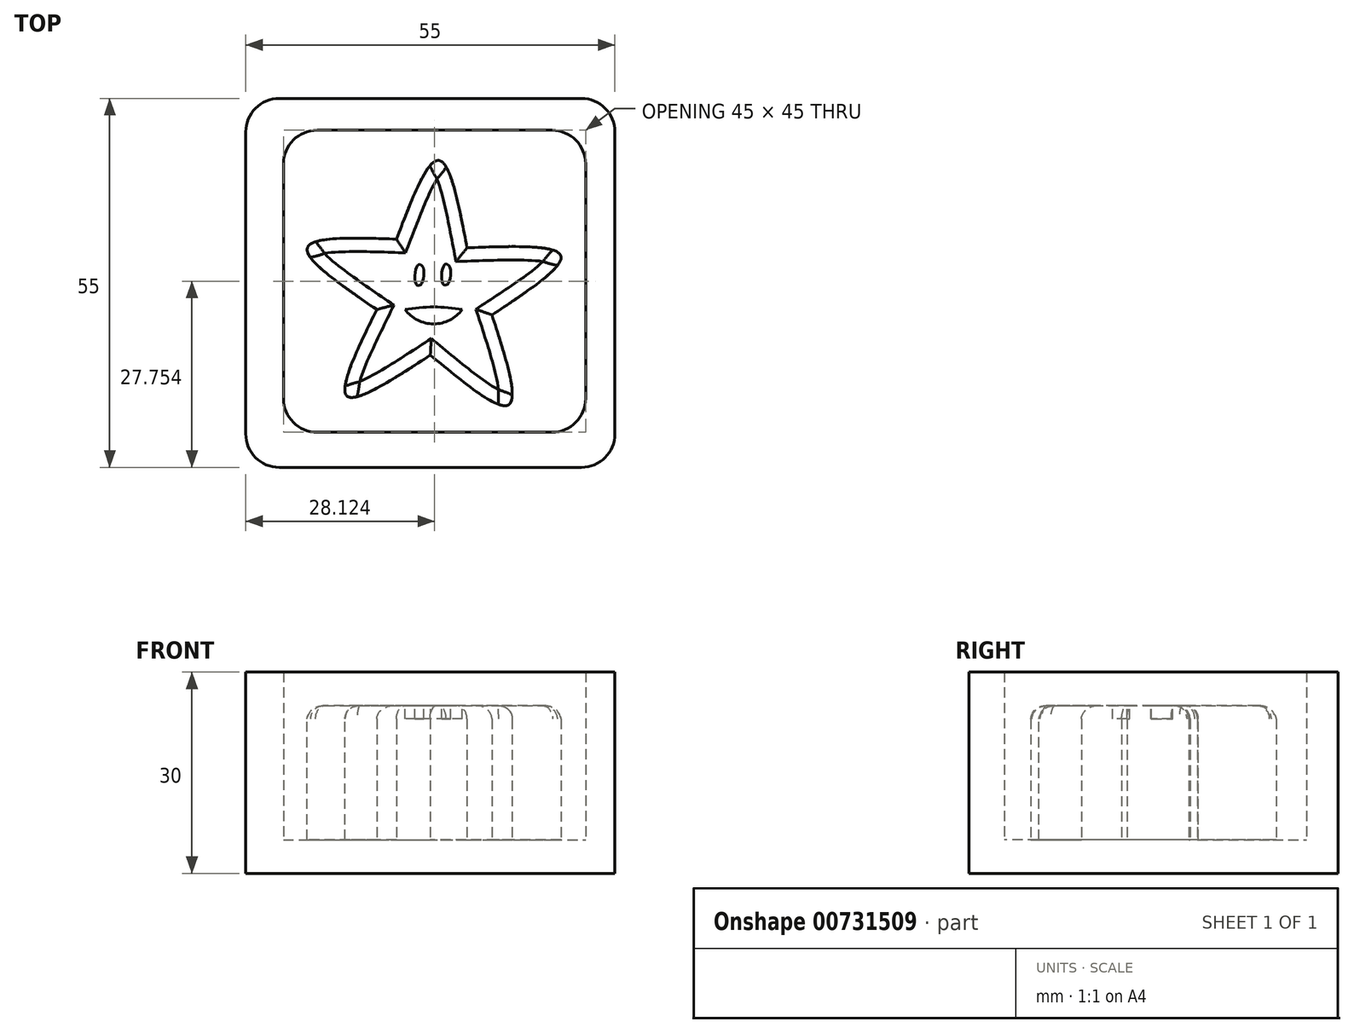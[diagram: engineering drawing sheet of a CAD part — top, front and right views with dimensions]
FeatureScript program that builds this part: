
annotation { "Feature Type Name" : "Feature", "Feature Type Description" : "" }
export const myFeature = defineFeature(function(context is Context, id is Id, definition is map)
    precondition{}
    {
        {
            var Q0;
            Q0=qCreatedBy(makeId("Top.planeOp"),FACE);
            var sketch = newSketch(context, id + "F0", { "sketchPlane" : qUnion([Q0])});
            skLineSegment(sketch, "E0.bottom", {"start": v(25, -20.84) * mm, "end": v(-25, -20.84) * mm});
            skLineSegment(sketch, "E0.top", {"start": v(25, 29.16) * mm, "end": v(-25, 29.16) * mm});
            skLineSegment(sketch, "E0.left", {"start": v(25, -20.84) * mm, "end": v(25, 29.16) * mm});
            skLineSegment(sketch, "E0.right", {"start": v(-25, -20.84) * mm, "end": v(-25, 29.16) * mm});
            skPoint(sketch, "E0.middle", {"position": v(0, 4.16) * mm});
            skSolve(sketch);
        }
        {
            var Q0;
            Q0 = qSketchRegion(id + "F0", true);
            extrude(context, id + "F1", {"entities" : qUnion([Q0]), "depth" : 5 * mm, "offsetDistance" : 25 * mm});
        }
        {
            var Q0;
            Q0=makeQuery(id+"F1.opExtrude","CAP_FACE",FACE,{"disambiguationData":[OSD([sQuery(id+"F0.wireOp",EDGE,"E0.bottom"),sQuery(id+"F0.wireOp",EDGE,"E0.top"),sQuery(id+"F0.wireOp",EDGE,"E0.left"),sQuery(id+"F0.wireOp",EDGE,"E0.right")])],"isStart":false});
            var sketch = newSketch(context, id + "F2", { "sketchPlane" : qUnion([Q0])});
            skFitSpline(sketch, "E1", {"points": [v(-5.06, 10.5) * mm, v(1.24, 22.23) * mm, v(5.46, 9.21) * mm], "startDerivative": vector(13.75, 35.91) * mm, "endDerivative": vector(7.31, -38.33) * mm});
            skFitSpline(sketch, "E2", {"points": [v(5.46, 9.21) * mm, v(19.44, 8) * mm, v(9.17, -0.8) * mm], "startDerivative": vector(39.9, 1.48) * mm, "endDerivative": vector(-32.7, -21.56) * mm});
            skFitSpline(sketch, "E3", {"points": [v(9.17, -0.8) * mm, v(11.68, -14.18) * mm, v(0, -6.8) * mm], "startDerivative": vector(12.08, -37.22) * mm, "endDerivative": vector(-30.37, 25.15) * mm});
            skFitSpline(sketch, "E4", {"points": [v(-5.06, 10.5) * mm, v(-18.32, 9.21) * mm, v(-7.98, 0) * mm], "startDerivative": vector(-38.48, 1.26) * mm, "endDerivative": vector(32.4, -22.2) * mm});
            skFitSpline(sketch, "E5", {"points": [v(-7.98, 0) * mm, v(-12.41, -12.88) * mm, v(0, -6.8) * mm], "startDerivative": vector(-17.27, -35.33) * mm, "endDerivative": vector(33.18, 21.68) * mm});
            skSolve(sketch);
        }
        {
            var Q0;
            Q0 = qSketchRegion(id + "F2", true);
            extrude(context, id + "F3", {"entities" : qUnion([Q0]), "operationType" : NewBodyOperationType.ADD, "depth" : 20 * mm, "offsetDistance" : 25 * mm});
        }
        {
            var Q0;
            Q0=makeQuery(id+"F3.opExtrude","CAP_EDGE",EDGE,{"disambiguationData":[OSD([sQuery(id+"F2.wireOp",EDGE,"E4")])],"isStart":false});
            var Q1;
            Q1=makeQuery(id+"F3.opExtrude","CAP_EDGE",EDGE,{"disambiguationData":[OSD([sQuery(id+"F2.wireOp",EDGE,"E5")])],"isStart":false});
            var Q2;
            Q2=makeQuery(id+"F3.opExtrude","CAP_EDGE",EDGE,{"disambiguationData":[OSD([sQuery(id+"F2.wireOp",EDGE,"E3")])],"isStart":false});
            var Q3;
            Q3=makeQuery(id+"F3.opExtrude","CAP_EDGE",EDGE,{"disambiguationData":[OSD([sQuery(id+"F2.wireOp",EDGE,"E2")])],"isStart":false});
            var Q4;
            Q4=makeQuery(id+"F3.opExtrude","CAP_EDGE",EDGE,{"disambiguationData":[OSD([sQuery(id+"F2.wireOp",EDGE,"E1")])],"isStart":false});
            fillet(context, id + "F4", {"entities" : qUnion([Q0, Q1, Q2, Q3, Q4]), "radius" : 2 * mm, "tangentPropagation" : true, "allowEdgeOverflow" : false});
        }
        {
            var Q0;
            Q0=qCreatedBy(makeId("Top.planeOp"),FACE);
            var sketch = newSketch(context, id + "F5", { "sketchPlane" : qUnion([Q0])});
            skLineSegment(sketch, "E6.bottom", {"start": v(27.5, -23.53) * mm, "end": v(-27.5, -23.53) * mm});
            skLineSegment(sketch, "E6.top", {"start": v(27.5, 31.47) * mm, "end": v(-27.5, 31.47) * mm});
            skLineSegment(sketch, "E6.left", {"start": v(27.5, -23.53) * mm, "end": v(27.5, 31.47) * mm});
            skLineSegment(sketch, "E6.right", {"start": v(-27.5, -23.53) * mm, "end": v(-27.5, 31.47) * mm});
            skPoint(sketch, "E6.middle", {"position": v(0, 3.97) * mm});
            skLineSegment(sketch, "E7.bottom", {"start": v(23.12, -18.28) * mm, "end": v(-21.88, -18.28) * mm});
            skLineSegment(sketch, "E7.top", {"start": v(23.12, 26.72) * mm, "end": v(-21.88, 26.72) * mm});
            skLineSegment(sketch, "E7.left", {"start": v(23.12, -18.28) * mm, "end": v(23.12, 26.72) * mm});
            skLineSegment(sketch, "E7.right", {"start": v(-21.88, -18.28) * mm, "end": v(-21.88, 26.72) * mm});
            skPoint(sketch, "E7.middle", {"position": v(0, 3.98) * mm});
            skSolve(sketch);
        }
        {
            var Q0;
            Q0 = qSketchRegion(id + "F5", true);
            extrude(context, id + "F6", {"entities" : qUnion([Q0]), "operationType" : NewBodyOperationType.ADD, "depth" : 30 * mm, "offsetDistance" : 25 * mm});
        }
        {
            var Q0;
            Q0=makeQuery(id+"F6.opExtrude","SWEPT_EDGE",EDGE,{"disambiguationData":[OSD([sQuery(id+"F5.wireOp",EDGE,"E7.top"),sQuery(id+"F5.wireOp",EDGE,"E7.left")])]});
            var Q1;
            Q1=makeQuery(id+"F6.opExtrude","SWEPT_EDGE",EDGE,{"disambiguationData":[OSD([sQuery(id+"F5.wireOp",EDGE,"E7.bottom"),sQuery(id+"F5.wireOp",EDGE,"E7.left")])]});
            var Q2;
            Q2=makeQuery(id+"F6.opExtrude","SWEPT_EDGE",EDGE,{"disambiguationData":[OSD([sQuery(id+"F5.wireOp",EDGE,"E7.top"),sQuery(id+"F5.wireOp",EDGE,"E7.right")])]});
            var Q3;
            Q3=makeQuery(id+"F6.opExtrude","SWEPT_EDGE",EDGE,{"disambiguationData":[OSD([sQuery(id+"F5.wireOp",EDGE,"E7.bottom"),sQuery(id+"F5.wireOp",EDGE,"E7.right")])]});
            fillet(context, id + "F7", {"entities" : qUnion([Q0, Q1, Q2, Q3]), "radius" : 5 * mm, "tangentPropagation" : true, "allowEdgeOverflow" : false});
        }
        {
            var Q0;
            Q0=makeQuery(id+"F6.opExtrude","SWEPT_EDGE",EDGE,{"disambiguationData":[OSD([sQuery(id+"F5.wireOp",EDGE,"E6.top"),sQuery(id+"F5.wireOp",EDGE,"E6.right")])]});
            var Q1;
            Q1=makeQuery(id+"F6.opExtrude","SWEPT_EDGE",EDGE,{"disambiguationData":[OSD([sQuery(id+"F5.wireOp",EDGE,"E6.top"),sQuery(id+"F5.wireOp",EDGE,"E6.left")])]});
            var Q2;
            Q2=makeQuery(id+"F6.opExtrude","SWEPT_EDGE",EDGE,{"disambiguationData":[OSD([sQuery(id+"F5.wireOp",EDGE,"E6.bottom"),sQuery(id+"F5.wireOp",EDGE,"E6.right")])]});
            var Q3;
            Q3=makeQuery(id+"F6.opExtrude","SWEPT_EDGE",EDGE,{"disambiguationData":[OSD([sQuery(id+"F5.wireOp",EDGE,"E6.bottom"),sQuery(id+"F5.wireOp",EDGE,"E6.left")])]});
            fillet(context, id + "F8", {"entities" : qUnion([Q0, Q1, Q2, Q3]), "radius" : 5 * mm, "tangentPropagation" : true, "allowEdgeOverflow" : false});
        }
        {
            var Q0;
            Q0=makeQuery(id+"F3.opExtrude","CAP_FACE",FACE,{"disambiguationData":[OSD([sQuery(id+"F2.wireOp",EDGE,"ea22f027-b894-4d35-ad94-6574a105fb3a"),sQuery(id+"F2.wireOp",EDGE,"02972ecb-89ef-400d-9b9c-b38da18b9f26"),sQuery(id+"F2.wireOp",EDGE,"d4665c4b-3644-410e-b7a9-793b46f9e3d8"),sQuery(id+"F2.wireOp",EDGE,"4904a858-6bfa-4176-8c43-c28e2eb22261"),sQuery(id+"F2.wireOp",EDGE,"281288f6-0dfc-4ab6-aa52-0887e6a29920"),sQuery(id+"F2.wireOp",EDGE,"e6a59349-29be-4dfa-85ae-5f5bb5e19001"),sQuery(id+"F2.wireOp",EDGE,"33865bf9-fee0-4887-a290-a33334908563"),sQuery(id+"F2.wireOp",EDGE,"b5a1ea3e-0a3a-46d1-a9d2-b11f3d4d393f"),sQuery(id+"F2.wireOp",EDGE,"9160b71b-1dbf-454e-b8aa-38d11ad0787a"),sQuery(id+"F2.wireOp",EDGE,"508b1097-dadd-43a8-a367-845bdcffccfe"),sQuery(id+"F2.wireOp",EDGE,"49bc861f-a654-40ca-8a3d-e641ddbf638b"),sQuery(id+"F2.wireOp",EDGE,"b91fa5d4-4bf4-43ae-99f3-f47139d4a982"),sQuery(id+"F2.wireOp",EDGE,"91c30a01-8c2e-4a9e-bc94-6af126d221bb"),sQuery(id+"F2.wireOp",EDGE,"46226220-93ab-4b08-822d-1d4fcd13f7f0"),sQuery(id+"F2.wireOp",EDGE,"3cccdf76-d96c-4aba-a423-c60eeaef6f2e"),sQuery(id+"F2.wireOp",EDGE,"a7a83c28-3530-49f8-9c53-c2483f9e7872"),sQuery(id+"F2.wireOp",EDGE,"bd418752-b331-4a27-85c2-437b8f3f9da8"),sQuery(id+"F2.wireOp",EDGE,"d86c6e9c-a8e8-46bc-9cbd-8a8ccbf43cd8"),sQuery(id+"F2.wireOp",EDGE,"18ce2d2a-cbe7-4d55-9af2-434ca90d4d8a"),sQuery(id+"F2.wireOp",EDGE,"3e9cf44d-97a5-4047-a5a6-f93e2a769566"),sQuery(id+"F2.wireOp",EDGE,"72104b77-425f-43ce-bfee-662c898d3039"),sQuery(id+"F2.wireOp",EDGE,"b0c94266-c951-4a47-ba1d-05842cc99b57"),sQuery(id+"F2.wireOp",EDGE,"a3bab185-7591-47d8-8c31-848ac42d466f"),sQuery(id+"F2.wireOp",EDGE,"95482d24-3030-4f51-9019-3cd7c5544abc"),sQuery(id+"F2.wireOp",EDGE,"ecb43bb9-7518-4037-82ed-3b3d48b88220"),sQuery(id+"F2.wireOp",EDGE,"6709acc4-015e-4cee-b4b1-e8162d60af49"),sQuery(id+"F2.wireOp",EDGE,"9c087dd5-8d5f-4c13-9bc7-0dec2b4ae27f"),sQuery(id+"F2.wireOp",EDGE,"1f7cd400-eb1a-477a-a8e0-1a1905c8875b"),sQuery(id+"F2.wireOp",EDGE,"2f4714a1-4b7a-4e27-a0f3-d2b64ee53851"),sQuery(id+"F2.wireOp",EDGE,"cf6d8417-590a-48c5-99af-b32b253a895c"),sQuery(id+"F2.wireOp",EDGE,"93dc3e3c-f9e4-4bb0-b6ea-1e3b1bb8eda1"),sQuery(id+"F2.wireOp",EDGE,"f410118d-9d75-4c7b-a8da-20c13fada343"),sQuery(id+"F2.wireOp",EDGE,"eae4d265-d466-4ba0-ad54-7133bb8090aa"),sQuery(id+"F2.wireOp",EDGE,"29f3a1ae-a44a-4252-90b8-49e4f717a763"),sQuery(id+"F2.wireOp",EDGE,"d95e87fc-c752-4cd3-ba2f-4e1b622d11e6"),sQuery(id+"F2.wireOp",EDGE,"42a256c7-bd9f-4b82-a40e-3aa7b43a7311"),sQuery(id+"F2.wireOp",EDGE,"5cccd7cb-d227-495f-bd2e-dd321fa3711f"),sQuery(id+"F2.wireOp",EDGE,"4779d78b-67a4-4074-8e1d-094c3c882748"),sQuery(id+"F2.wireOp",EDGE,"d78c889f-446d-499c-940c-2d769212d2d6"),sQuery(id+"F2.wireOp",EDGE,"5978d452-f883-4c3a-89cf-e77a3d4812d3"),sQuery(id+"F2.wireOp",EDGE,"d596c75f-4af1-4a7b-b4a9-307fc33695f2"),sQuery(id+"F2.wireOp",EDGE,"ac6da6d2-c422-4b3f-ab3b-024f16e2174f"),sQuery(id+"F2.wireOp",EDGE,"f701fbac-f9f2-41ce-b398-1cdb972a07c6"),sQuery(id+"F2.wireOp",EDGE,"6ea0370e-b9df-47c8-82b6-4bf531107383"),sQuery(id+"F2.wireOp",EDGE,"93d4d691-acf9-4093-813e-c243a6abfd77"),sQuery(id+"F2.wireOp",EDGE,"564c231c-7281-4956-8916-2b9847646294"),sQuery(id+"F2.wireOp",EDGE,"447afba2-fe07-4bf1-a098-a2fa503544db"),sQuery(id+"F2.wireOp",EDGE,"783018d8-4da7-439e-baff-4ea1af6aeaae"),sQuery(id+"F2.wireOp",EDGE,"23360fc8-9112-4eab-be8c-d36215a4c504"),sQuery(id+"F2.wireOp",EDGE,"f39823fe-76bf-4b28-8de3-5866c156ca6e"),sQuery(id+"F2.wireOp",EDGE,"94261188-8fe8-4fe3-9cfb-41c0c768c078"),sQuery(id+"F2.wireOp",EDGE,"639eefb3-3c81-4241-8da9-6294a00eecad"),sQuery(id+"F2.wireOp",EDGE,"63a26b51-3e8c-4d7f-a8c5-c852ed6635fd"),sQuery(id+"F2.wireOp",EDGE,"0cbcce5a-d863-44dc-85fc-889f0cb27286"),sQuery(id+"F2.wireOp",EDGE,"41481716-7baf-47e6-bab9-346e36ad7ed7"),sQuery(id+"F2.wireOp",EDGE,"a0ece215-4608-46fb-b9de-0966884f3722"),sQuery(id+"F2.wireOp",EDGE,"cea85d6a-f16e-43e1-82ab-1eb20eedc667"),sQuery(id+"F2.wireOp",EDGE,"90b3652e-c92f-4129-b232-5fc3862136ad"),sQuery(id+"F2.wireOp",EDGE,"d85ff010-6106-4afe-aa78-55669356d399"),sQuery(id+"F2.wireOp",EDGE,"7b3810e8-a3aa-46c5-9845-10c95717e511"),sQuery(id+"F2.wireOp",EDGE,"32d08b1a-e728-49a8-914d-c4ecc0554df0"),sQuery(id+"F2.wireOp",EDGE,"a932f2cb-edb6-4d43-8a31-36080f450e31"),sQuery(id+"F2.wireOp",EDGE,"6d77b220-5459-4ded-ba71-0805bf8e97fe"),sQuery(id+"F2.wireOp",EDGE,"d4a3d79f-eb9b-45d3-af4d-7f6e0c1d0b6a"),sQuery(id+"F2.wireOp",EDGE,"3a8167d0-93d4-4fee-93fc-e765f78cc71a"),sQuery(id+"F2.wireOp",EDGE,"275b4ef8-3749-467f-b8de-4c5ca6efd012"),sQuery(id+"F2.wireOp",EDGE,"250f3aee-73fb-4a09-89d3-a25958f34bab"),sQuery(id+"F2.wireOp",EDGE,"6f7494f2-175a-490b-9ca9-9ab7524c1492"),sQuery(id+"F2.wireOp",EDGE,"d4bde236-d2fc-4dbc-ba9a-6cd55d3f6a15"),sQuery(id+"F2.wireOp",EDGE,"989c9d0c-4ceb-449c-bc73-c96cc92b2f1a"),sQuery(id+"F2.wireOp",EDGE,"78fda69b-8c10-4e3c-872b-102a69ddef83"),sQuery(id+"F2.wireOp",EDGE,"a15857fb-2d82-4afa-8e36-ecf18161f336"),sQuery(id+"F2.wireOp",EDGE,"b5dc66a1-7abf-40bc-8f4a-394b90f8d275"),sQuery(id+"F2.wireOp",EDGE,"03030db5-3b63-482b-9307-c4991d58ca64"),sQuery(id+"F2.wireOp",EDGE,"17e9b168-3d8f-465c-93a2-82195902c407"),sQuery(id+"F2.wireOp",EDGE,"7465df75-a5ab-45e8-a90a-397120fadcc2"),sQuery(id+"F2.wireOp",EDGE,"16613f2c-828e-433e-977f-464dc0bab4c5"),sQuery(id+"F2.wireOp",EDGE,"47fe3ba8-9260-47cb-bf79-68fdcf4e78a0"),sQuery(id+"F2.wireOp",EDGE,"43b05b75-3a74-4bef-b5f9-64ce1e4d3f92"),sQuery(id+"F2.wireOp",EDGE,"991257b0-d842-40bd-a016-b0dcd5567a51"),sQuery(id+"F2.wireOp",EDGE,"bb4ff494-dc7b-4f0b-a60d-949d5af28021"),sQuery(id+"F2.wireOp",EDGE,"be03492f-4681-4838-bb13-d5d06ba2e1d7"),sQuery(id+"F2.wireOp",EDGE,"97411946-2583-4f17-b8cd-8f9e6a677e8b"),sQuery(id+"F2.wireOp",EDGE,"e440f547-cbda-46c2-b9d7-514191ae65e8"),sQuery(id+"F2.wireOp",EDGE,"60f7c09c-a596-4b98-aa55-1e6369aacef9"),sQuery(id+"F2.wireOp",EDGE,"234aff2d-32ac-438c-92f5-d0bf77c84f1a"),sQuery(id+"F2.wireOp",EDGE,"b87faba7-c0e6-491b-a4a2-d00cc7015cd8"),sQuery(id+"F2.wireOp",EDGE,"90d1a113-3cec-4f00-adab-2e55525ea2b2"),sQuery(id+"F2.wireOp",EDGE,"979cd316-eb47-42a9-a592-d31acdb67cec"),sQuery(id+"F2.wireOp",EDGE,"7428ea2a-103f-4ebb-b4b8-c831fed82aef"),sQuery(id+"F2.wireOp",EDGE,"52370307-3d29-4edd-afa2-faff63602114"),sQuery(id+"F2.wireOp",EDGE,"88128a0f-d6ec-4b0a-bc8b-e0f4bc7cf75c"),sQuery(id+"F2.wireOp",EDGE,"7de87fd6-0158-4915-807c-9afae7a70aa2"),sQuery(id+"F2.wireOp",EDGE,"180d38d7-08b5-478e-9bbb-86c7c12d8af8"),sQuery(id+"F2.wireOp",EDGE,"22979340-1db9-4cf8-9821-84e582c46be2"),sQuery(id+"F2.wireOp",EDGE,"2aecfa87-5c26-43c7-b01b-42edbaea5f26"),sQuery(id+"F2.wireOp",EDGE,"d53a2147-7160-4d9c-aa38-cbb9aa0cbb9e"),sQuery(id+"F2.wireOp",EDGE,"197ff192-98b0-49e9-9c6a-db6e28c6daef"),sQuery(id+"F2.wireOp",EDGE,"ee9a66c0-ba42-4615-a1e3-135759764a0c"),sQuery(id+"F2.wireOp",EDGE,"111631f7-a570-4717-906c-35496458c016"),sQuery(id+"F2.wireOp",EDGE,"bb98202e-b631-4bd4-8df0-c97bad7516e4"),sQuery(id+"F2.wireOp",EDGE,"78248693-6aa8-4cc8-8159-669be31d40dc"),sQuery(id+"F2.wireOp",EDGE,"0797b34a-24f6-40f6-be44-cc817c5cdd3a"),sQuery(id+"F2.wireOp",EDGE,"9025d657-ca05-4ccc-ab26-e4792d65176a"),sQuery(id+"F2.wireOp",EDGE,"3aceb39b-8709-4280-877c-cd3977029748"),sQuery(id+"F2.wireOp",EDGE,"95408ccb-4e7c-4662-8e89-42555b2ea574"),sQuery(id+"F2.wireOp",EDGE,"c1b7ed67-20c2-4104-afb5-83cdaba9b995"),sQuery(id+"F2.wireOp",EDGE,"688e50f1-9262-4d49-9aba-93f33a78428b"),sQuery(id+"F2.wireOp",EDGE,"5589d507-3ac0-4531-9f5c-d9aafc032d42"),sQuery(id+"F2.wireOp",EDGE,"814193a2-ae33-43cb-ab67-dd1ad4c57dc9"),sQuery(id+"F2.wireOp",EDGE,"bd3d597c-a3a3-4bdb-b489-a50847514c41"),sQuery(id+"F2.wireOp",EDGE,"f9c765e2-3d02-412e-b5c8-9cbecb79335e"),sQuery(id+"F2.wireOp",EDGE,"5374216d-eb8c-473a-b232-3210bd6322dc"),sQuery(id+"F2.wireOp",EDGE,"78cd440d-3889-43df-8524-f9ef943d22b7"),sQuery(id+"F2.wireOp",EDGE,"f48db664-ea3d-465f-be7b-7c3f43ebaf76"),sQuery(id+"F2.wireOp",EDGE,"9b5eb5e8-1bde-4125-a0ae-612cc48788f3"),sQuery(id+"F2.wireOp",EDGE,"067b160c-a63e-427f-8b16-299480079f5a"),sQuery(id+"F2.wireOp",EDGE,"672eeee8-6e70-47e9-8364-98da75f5d819"),sQuery(id+"F2.wireOp",EDGE,"5127b20d-0d7c-46bc-be36-6cdcb1b18aaa"),sQuery(id+"F2.wireOp",EDGE,"56f0d7d5-69bd-4014-ad11-0b63b564c3d5"),sQuery(id+"F2.wireOp",EDGE,"9f1370dc-adc3-4c9f-a706-93b7f0c65285"),sQuery(id+"F2.wireOp",EDGE,"4b75f99a-66c5-4a90-8e02-9a1d458dee98"),sQuery(id+"F2.wireOp",EDGE,"d4360ca9-398d-4564-a7bb-61c3d18fbd84"),sQuery(id+"F2.wireOp",EDGE,"57885f1f-bfc3-4972-9dac-58e4406466f0"),sQuery(id+"F2.wireOp",EDGE,"85ac6021-34b8-4ad9-a652-f7b15531d4a2"),sQuery(id+"F2.wireOp",EDGE,"7a21dffe-2b5b-45e4-9271-5292728f147a"),sQuery(id+"F2.wireOp",EDGE,"E1"),sQuery(id+"F2.wireOp",EDGE,"E2"),sQuery(id+"F2.wireOp",EDGE,"E3"),sQuery(id+"F2.wireOp",EDGE,"E4"),sQuery(id+"F2.wireOp",EDGE,"E5")])],"isStart":false});
            var sketch = newSketch(context, id + "F9", { "sketchPlane" : qUnion([Q0])});
            skFitSpline(sketch, "E8", {"points": [v(-1.06, 6.23) * mm, v(-1.6, 6.72) * mm, v(-2.06, 6.33) * mm, v(-2.16, 3.87) * mm, v(-1.66, 3.6) * mm, v(-1.2, 4.07) * mm, v(-1.06, 6.23) * mm]});
            skFitSpline(sketch, "E9", {"points": [v(2.92, 6.29) * mm, v(2.39, 6.79) * mm, v(1.92, 6.39) * mm, v(1.82, 3.93) * mm, v(2.32, 3.67) * mm, v(2.78, 4.13) * mm, v(2.92, 6.29) * mm]});
            skArc(sketch, "E10", {"start": v(-3.77, 0) * mm, "mid": v(0.5, -2.13) * mm, "end": v(4.76, 0) * mm});
            skArc(sketch, "E11", {"start": v(4.76, 0) * mm, "mid": v(0.5, 0.38) * mm, "end": v(-3.77, 0) * mm});
            skArc(sketch, "E12", {"start": v(3.2, -1.39) * mm, "mid": v(0.61, -0.99) * mm, "end": v(-1.95, -1.54) * mm});
            skSolve(sketch);
        }
        {
            var Q0;
            Q0=makeQuery(id+"F9.imprint","IMPRINT",FACE,{"disambiguationData":[TD([[makeQuery(id+"F9.imprint","IMPRINT",EDGE,{"derivedFrom":sQuery(id+"F9.wireOp",EDGE,"E8")}),1.0]])]});
            var Q1;
            Q1=makeQuery(id+"F9.imprint","IMPRINT",FACE,{"disambiguationData":[TD([[makeQuery(id+"F9.imprint","IMPRINT",EDGE,{"derivedFrom":sQuery(id+"F9.wireOp",EDGE,"E9")}),1.0]])]});
            var Q2;
            {var subQ6=sQuery(id+"F9.wireOp",EDGE,"E12");Q2=makeQuery(id+"F9.imprint","IMPRINT",FACE,{"disambiguationData":[TD([[makeQuery(id+"F9.imprint","IMPRINT",EDGE,{"derivedFrom":subQ6}),-1.0]])]});}
            var Q3;
            {var subQ0=sQuery(id+"F9.wireOp",EDGE,"E12");Q3=makeQuery(id+"F9.imprint","IMPRINT",FACE,{"disambiguationData":[TD([[makeQuery(id+"F9.imprint","IMPRINT",EDGE,{"derivedFrom":subQ0}),1.0]])]});}
            var Q4;
            Q4=makeQuery(id+"F9.imprint","IMPRINT",FACE,{"disambiguationData":[TD([[makeQuery(id+"F9.imprint","IMPRINT",EDGE,{"derivedFrom":makeQuery(id+"F3.opExtrude","CAP_EDGE",EDGE,{"disambiguationData":[OSD([sQuery(id+"F2.wireOp",EDGE,"ea22f027-b894-4d35-ad94-6574a105fb3a")])],"isStart":false})}),1.0]])]});
            extrude(context, id + "F10", {"entities" : qUnion([Q0, Q1, Q2, Q3, Q4]), "operationType" : NewBodyOperationType.REMOVE, "oppositeDirection" : true, "depth" : 2 * mm, "offsetDistance" : 25 * mm});
        }
    });
